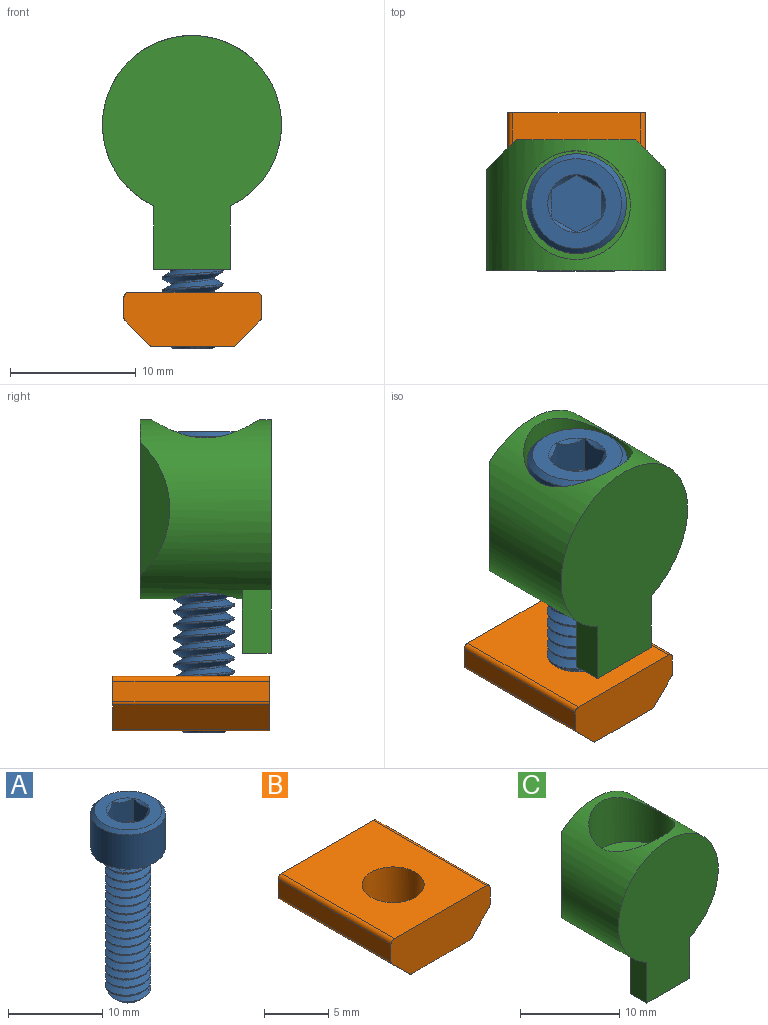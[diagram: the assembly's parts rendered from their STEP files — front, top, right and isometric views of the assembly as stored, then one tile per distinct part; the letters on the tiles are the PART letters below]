
ASSEMBLY  parts=3 mates=3
PART A: 23 faces, bbox 8.3x8.3x24.7 mm
  f0: cylinder r=2.41mm len=18.25mm, axis (0,0,1), area 34.7mm2, adj f1,f2,f4,f8
  f1: bspline ~20.01x4.94mm, area 181.7mm2, adj f0,f3,f4,f8
  f2: bspline ~19.48x4.94mm, area 181.9mm2, adj f0,f3,f4,f8
  f3: cylinder r=1.73mm len=18.94mm, axis (0,0,1), area 25.8mm2, adj f1,f2,f4,f8
  f4: cone r=1.61mm half-angle=45deg, axis (0,0,1), area 7.8mm2, adj f0,f1,f2,f3,f5
  f5: plane 3.22x3.22mm, normal (0,0,-1), area 8.2mm2, adj f4
  f6: cylinder r=3.96mm len=7.92mm, axis (0,0,-1), area 110.3mm2, adj f8,f22
  f7: plane 7.13x7.13mm, normal (0,0,1), area 23.5mm2, adj f9,f10,f11,f12,f13,f14,f22
  f8: plane 8.33x8.33mm, normal (0,0,-1), area 35.7mm2, adj f0,f1,f2,f3,f6
  f9: cone r=2.29mm half-angle=45deg, axis (0,0,1), area 0.7mm2, adj f7,f16
  f10: cone r=2.29mm half-angle=45deg, axis (0,0,1), area 0.7mm2, adj f7,f17
  f11: cone r=2.29mm half-angle=45deg, axis (0,0,1), area 0.7mm2, adj f7,f18
  f12: cone r=2.29mm half-angle=45deg, axis (0,0,1), area 0.7mm2, adj f7,f19
  f13: cone r=2.29mm half-angle=45deg, axis (0,0,1), area 0.7mm2, adj f7,f20
  f14: cone r=2.29mm half-angle=45deg, axis (0,0,1), area 0.7mm2, adj f7,f21
  f15: plane 4.58x3.97mm, normal (0,0,1), area 13.6mm2, adj f16,f17,f18,f19,f20,f21
  f16: plane 2.98x1.98mm, normal (0.5,-0.87,0), area 6.4mm2, adj f9,f15,f17,f21
  f17: plane 2.98x2.3mm, normal (1,0,0), area 6.4mm2, adj f10,f15,f16,f18
  f18: plane 2.98x1.98mm, normal (0.5,0.87,0), area 6.4mm2, adj f11,f15,f17,f19
  f19: plane 2.98x1.98mm, normal (-0.5,0.87,0), area 6.4mm2, adj f12,f15,f18,f20
  f20: plane 2.98x2.3mm, normal (-1,0,0), area 6.4mm2, adj f13,f15,f19,f21
  f21: plane 2.98x1.98mm, normal (-0.5,-0.87,0), area 6.4mm2, adj f14,f15,f16,f20
  f22: cone r=3.57mm half-angle=45deg, axis (0,0,-1), area 13.3mm2, adj f6,f7
PART B: 15 faces, bbox 10.9x12.4x4.3 mm
  f0: plane 12.45x1.94mm, normal (-0.71,0,-0.71), area 34.1mm2, adj f6,f7,f10,f13
  f1: plane 12.45x1.62mm, normal (-1,0,0), area 20.2mm2, adj f6,f7,f13,f14
  f2: plane 12.45x10.16mm, normal (0,0,1), area 108.2mm2, adj f6,f7,f8,f12,f14
  f3: plane 12.45x1.62mm, normal (1,0,0), area 20.2mm2, adj f6,f7,f11,f12
  f4: plane 12.45x1.94mm, normal (0.71,0,-0.71), area 34.1mm2, adj f6,f7,f9,f11
  f5: plane 12.45x6.29mm, normal (0,0,-1), area 60mm2, adj f6,f7,f8,f9,f10
  f6: plane 10.92x4.32mm, normal (0,1,0), area 42.4mm2, adj f0,f1,f2,f3,f4,f5,f9,f10
  f7: plane 10.92x4.32mm, normal (0,-1,0), area 42.4mm2, adj f0,f1,f2,f3,f4,f5,f9,f10
  f8: cylinder r=2.41mm len=4.83mm, axis (0,0,1), area 65.5mm2, adj f2,f5
  f9: cylinder r=0.38mm len=12.45mm, axis (0,-1,0), area 3.7mm2, adj f4,f5,f6,f7
  f10: cylinder r=0.38mm len=12.45mm, axis (0,-1,0), area 3.7mm2, adj f0,f5,f6,f7
  f11: cylinder r=0.38mm len=12.45mm, axis (0,-1,0), area 3.7mm2, adj f3,f4,f6,f7
  f12: cylinder r=0.38mm len=12.45mm, axis (0,-1,0), area 7.4mm2, adj f2,f3,f6,f7
  f13: cylinder r=0.38mm len=12.45mm, axis (0,-1,0), area 3.7mm2, adj f0,f1,f6,f7
  f14: cylinder r=0.38mm len=12.45mm, axis (0,-1,0), area 7.4mm2, adj f1,f2,f6,f7
PART C: 12 faces, bbox 14.2x10.4x18.6 mm
  f0: cylinder r=7.11mm len=14.22mm, axis (0,1,0), area 331.4mm2, adj f1,f2,f3,f5,f6,f7,f8,f9
  f1: plane 18.57x14.22mm, normal (0,-1,0), area 186.7mm2, adj f0,f3,f4,f5
  f2: plane 14.22x9.5mm, normal (0,1,0), area 124.3mm2, adj f0,f7,f8
  f3: plane 5.03x2.29mm, normal (1,0,0), area 11.5mm2, adj f0,f1,f4,f6
  f4: plane 6.09x2.29mm, normal (0,0,-1), area 13.9mm2, adj f1,f3,f5,f6
  f5: plane 5.03x2.29mm, normal (-1,0,0), area 11.5mm2, adj f0,f1,f4,f6
  f6: plane 6.09x5.03mm, normal (0,1,0), area 27.8mm2, adj f0,f3,f4,f5
  f7: plane 10.59x2.36mm, normal (-0.71,0.71,0), area 24.5mm2, adj f0,f2
  f8: plane 10.59x2.36mm, normal (0.71,0.71,0), area 24.5mm2, adj f0,f2
  f9: cylinder r=4.32mm len=8.64mm, axis (0,0,-1), area 138.6mm2, adj f0,f10
  f10: plane 8.64x8.64mm, normal (0,0,1), area 38.3mm2, adj f9,f11
  f11: cylinder r=2.54mm len=8.41mm, axis (0,0,1), area 130.5mm2, adj f0,f10
PLACE A t=(0.05,0.12,0)mm
PLACE B t=(0.05,0.12,-0.72)mm
PLACE C at identity fixed
MATE cylindrical B.f8 <-> A.f0  axis (0,0,1) through (0.05,0.12,-14.59)mm
MATE parallel B.f3 <-> C.f3  axis (1,0,0) through (5.51,1.14,-15.78)mm
MATE fastened A.f8 <-> C.f9  axis (0,0,-1) through (0,0,0)mm
